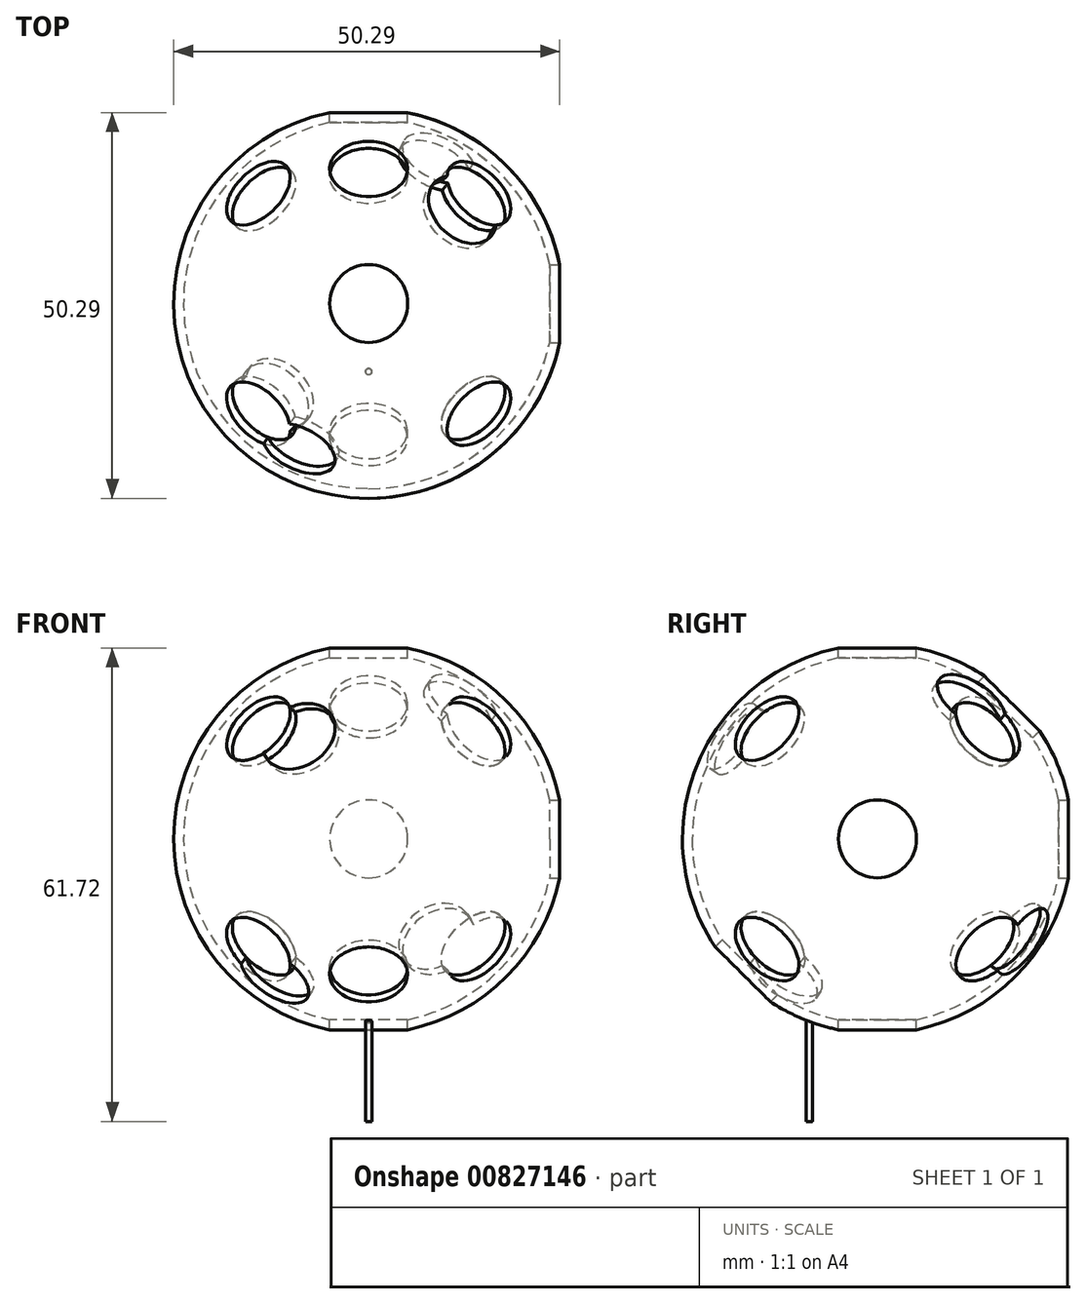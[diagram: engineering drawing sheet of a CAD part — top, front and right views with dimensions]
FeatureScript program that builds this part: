
annotation { "Feature Type Name" : "Feature", "Feature Type Description" : "" }
export const myFeature = defineFeature(function(context is Context, id is Id, definition is map)
    precondition{}
    {
        {
            assignVariable(context, id + "F0", {"name" : "SphereDiameter", "anyValue" : 2});
        }
        {
            var Q0;
            Q0=qCreatedBy(makeId("Top.planeOp"),FACE);
            var sketch = newSketch(context, id + "F1", { "sketchPlane" : qUnion([Q0])});
            skArc(sketch, "E0", {"start": v(0, 25.4) * mm, "mid": v(-25.4, 0) * mm, "end": v(0, -25.4) * mm});
            skLineSegment(sketch, "E1", {"start": v(0, 25.4) * mm, "end": v(0, -25.4) * mm});
            skSolve(sketch);
        }
        {
            var Q0;
            Q0=qSketchRegion(id+"F1",true);
            var Q1;
            Q1=sQuery(id+"F1.wireOp",EDGE,"E1");
            revolve(context, id + "F2", {"surfaceOperationType" : NewSurfaceOperationType.NEW, "entities" : qUnion([Q0]), "axis" : qUnion([Q1]), "revolveType" : RevolveType.FULL});
        }
        {
            var Q0;
            Q0=qCreatedBy(makeId("Top.planeOp"),FACE);
            var sketch = newSketch(context, id + "F3", { "sketchPlane" : qUnion([Q0])});
            skLineSegment(sketch, "E2", {"start": v(0, 0) * mm, "end": v(0, 25.4) * mm});
            skLineSegment(sketch, "E3", {"start": v(0, 0) * mm, "end": v(0, -25.4) * mm});
            skLineSegment(sketch, "E4", {"start": v(0, 0) * mm, "end": v(25.4, 0) * mm});
            skLineSegment(sketch, "E5", {"start": v(0, 0) * mm, "end": v(-25.4, 0) * mm});
            skSolve(sketch);
        }
        {
            var Q0;
            Q0=qCreatedBy(makeId("Front.planeOp"),FACE);
            var sketch = newSketch(context, id + "F4", { "sketchPlane" : qUnion([Q0])});
            skLineSegment(sketch, "E6", {"start": v(0, 0) * mm, "end": v(0, 25.4) * mm});
            skLineSegment(sketch, "E7", {"start": v(0, 0) * mm, "end": v(0, -25.4) * mm});
            skSolve(sketch);
        }
        {
            var Q0;
            Q0=sQuery(id+"F4.wireOp",VERTEX,"E6.end");
            var Q1;
            Q1=sQuery(id+"F3.wireOp",VERTEX,"E3.end");
            var Q2;
            Q2=sQuery(id+"F3.wireOp",VERTEX,"E4.end");
            cPlane(context, id + "F5", {"entities" : qUnion([Q0, Q1, Q2]), "cplaneType" : CPlaneType.THREE_POINT, "offset" : 25.4 * mm, "width" : 152.4 * mm, "height" : 152.4 * mm});
        }
        {
            var Q0;
            Q0=qCreatedBy(id+"F5.planeOp",FACE);
            var sketch = newSketch(context, id + "F6", { "sketchPlane" : qUnion([Q0])});
            skLineSegment(sketch, "E8", {"start": v(-20.74, 0) * mm, "end": v(10.37, -17.96) * mm});
            skLineSegment(sketch, "E9", {"start": v(10.37, -17.96) * mm, "end": v(10.37, 17.96) * mm});
            skLineSegment(sketch, "E10", {"start": v(10.37, 17.96) * mm, "end": v(-20.74, 0) * mm});
            skLineSegment(sketch, "E11", {"start": v(10.37, 17.96) * mm, "end": v(0, 0) * mm});
            skSolve(sketch);
        }
        {
            var Q0;
            Q0=sQuery(id+"F4.wireOp",VERTEX,"E6.end");
            var Q1;
            Q1=sQuery(id+"F6.wireOp",VERTEX,"E11.end");
            var Q2;
            Q2=sQuery(id+"F3.wireOp",VERTEX,"E3.start");
            cPlane(context, id + "F7", {"entities" : qUnion([Q0, Q1, Q2]), "cplaneType" : CPlaneType.THREE_POINT, "offset" : 25.4 * mm, "width" : 152.4 * mm, "height" : 152.4 * mm});
        }
        {
            var Q0;
            Q0=qCreatedBy(id+"F7.planeOp",FACE);
            var sketch = newSketch(context, id + "F8", { "sketchPlane" : qUnion([Q0])});
            skLineSegment(sketch, "E12", {"start": v(0, 0) * mm, "end": v(11.97, 8.47) * mm});
            skLineSegment(sketch, "E13", {"start": v(10.37, 7.33) * mm, "end": v(11.97, 8.47) * mm});
            skLineSegment(sketch, "E14", {"start": v(0, 0) * mm, "end": v(-10.37, -7.33) * mm});
            skSolve(sketch);
        }
        {
            var Q0;
            Q0=sQuery(id+"F3.wireOp",VERTEX,"E2.end");
            var Q1;
            Q1=sQuery(id+"F4.wireOp",VERTEX,"E6.end");
            var Q2;
            Q2=sQuery(id+"F3.wireOp",VERTEX,"E5.end");
            cPlane(context, id + "F9", {"entities" : qUnion([Q0, Q1, Q2]), "cplaneType" : CPlaneType.THREE_POINT, "offset" : 25.4 * mm, "width" : 152.4 * mm, "height" : 152.4 * mm});
        }
        {
            var Q0;
            Q0=qCreatedBy(id+"F9.planeOp",FACE);
            var sketch = newSketch(context, id + "F10", { "sketchPlane" : qUnion([Q0])});
            skLineSegment(sketch, "E15", {"start": v(20.74, 0) * mm, "end": v(-10.37, 17.96) * mm});
            skLineSegment(sketch, "E16", {"start": v(-10.37, 17.96) * mm, "end": v(-10.37, -17.96) * mm});
            skLineSegment(sketch, "E17", {"start": v(-10.37, -17.96) * mm, "end": v(20.74, 0) * mm});
            skLineSegment(sketch, "E18", {"start": v(-10.37, 17.96) * mm, "end": v(0, 0) * mm});
            skSolve(sketch);
        }
        {
            var Q0;
            Q0=sQuery(id+"F4.wireOp",VERTEX,"E6.end");
            var Q1;
            Q1=qCreatedBy(makeId("Origin.pointOp"),VERTEX);
            var Q2;
            Q2=sQuery(id+"F10.wireOp",VERTEX,"E18.end");
            cPlane(context, id + "F11", {"entities" : qUnion([Q0, Q1, Q2]), "cplaneType" : CPlaneType.THREE_POINT, "offset" : 25.4 * mm, "width" : 152.4 * mm, "height" : 152.4 * mm});
        }
        {
            var Q0;
            Q0=qCreatedBy(id+"F11.planeOp",FACE);
            var sketch = newSketch(context, id + "F12", { "sketchPlane" : qUnion([Q0])});
            skLineSegment(sketch, "E19", {"start": v(0, 0) * mm, "end": v(-11.97, 8.47) * mm});
            skLineSegment(sketch, "E20", {"start": v(-11.97, 8.47) * mm, "end": v(-10.37, 7.33) * mm});
            skLineSegment(sketch, "E21", {"start": v(10.37, -7.33) * mm, "end": v(0, 0) * mm});
            skSolve(sketch);
        }
        {
            var Q0;
            Q0=sQuery(id+"F3.wireOp",VERTEX,"E2.end");
            var Q1;
            Q1=sQuery(id+"F4.wireOp",VERTEX,"E7.end");
            var Q2;
            Q2=sQuery(id+"F3.wireOp",VERTEX,"E4.end");
            cPlane(context, id + "F13", {"entities" : qUnion([Q0, Q1, Q2]), "cplaneType" : CPlaneType.THREE_POINT, "offset" : 25.4 * mm, "width" : 152.4 * mm, "height" : 152.4 * mm});
        }
        {
            var Q0;
            Q0=qCreatedBy(id+"F13.planeOp",FACE);
            var sketch = newSketch(context, id + "F14", { "sketchPlane" : qUnion([Q0])});
            skLineSegment(sketch, "E22", {"start": v(10.37, -17.96) * mm, "end": v(10.37, 17.96) * mm});
            skLineSegment(sketch, "E23", {"start": v(10.37, 17.96) * mm, "end": v(-20.74, 0) * mm});
            skLineSegment(sketch, "E24", {"start": v(-20.74, 0) * mm, "end": v(10.37, -17.96) * mm});
            skLineSegment(sketch, "E25", {"start": v(10.37, 17.96) * mm, "end": v(0, 0) * mm});
            skSolve(sketch);
        }
        {
            var Q0;
            Q0=sQuery(id+"F3.wireOp",VERTEX,"E3.start");
            var Q1;
            Q1=sQuery(id+"F3.wireOp",VERTEX,"E2.end");
            var Q2;
            Q2=sQuery(id+"F14.wireOp",VERTEX,"E25.end");
            cPlane(context, id + "F15", {"entities" : qUnion([Q0, Q1, Q2]), "cplaneType" : CPlaneType.THREE_POINT, "offset" : 25.4 * mm, "width" : 152.4 * mm, "height" : 152.4 * mm});
        }
        {
            var Q0;
            Q0=qCreatedBy(id+"F15.planeOp",FACE);
            var sketch = newSketch(context, id + "F16", { "sketchPlane" : qUnion([Q0])});
            skLineSegment(sketch, "E26", {"start": v(0, 0) * mm, "end": v(8.47, -11.97) * mm});
            skLineSegment(sketch, "E27", {"start": v(7.33, -10.37) * mm, "end": v(8.47, -11.97) * mm});
            skLineSegment(sketch, "E28", {"start": v(0, 0) * mm, "end": v(-7.33, 10.37) * mm});
            skSolve(sketch);
        }
        {
            var Q0;
            Q0=sQuery(id+"F4.wireOp",VERTEX,"E6.end");
            var Q1;
            Q1=sQuery(id+"F3.wireOp",VERTEX,"E4.end");
            var Q2;
            Q2=sQuery(id+"F3.wireOp",VERTEX,"E2.end");
            cPlane(context, id + "F17", {"entities" : qUnion([Q0, Q1, Q2]), "cplaneType" : CPlaneType.THREE_POINT, "offset" : 25.4 * mm, "width" : 152.4 * mm, "height" : 152.4 * mm});
        }
        {
            var Q0;
            Q0=qCreatedBy(id+"F17.planeOp",FACE);
            var sketch = newSketch(context, id + "F18", { "sketchPlane" : qUnion([Q0])});
            skLineSegment(sketch, "E29", {"start": v(-10.37, 17.96) * mm, "end": v(20.74, 0) * mm});
            skLineSegment(sketch, "E30", {"start": v(20.74, 0) * mm, "end": v(-10.37, -17.96) * mm});
            skLineSegment(sketch, "E31", {"start": v(-10.37, -17.96) * mm, "end": v(-10.37, 17.96) * mm});
            skLineSegment(sketch, "E32", {"start": v(-10.37, 17.96) * mm, "end": v(0, 0) * mm});
            skSolve(sketch);
        }
        {
            var Q0;
            Q0=sQuery(id+"F4.wireOp",VERTEX,"E6.end");
            var Q1;
            Q1=sQuery(id+"F18.wireOp",VERTEX,"E32.end");
            var Q2;
            Q2=sQuery(id+"F3.wireOp",VERTEX,"E3.start");
            cPlane(context, id + "F19", {"entities" : qUnion([Q0, Q1, Q2]), "cplaneType" : CPlaneType.THREE_POINT, "offset" : 25.4 * mm, "width" : 152.4 * mm, "height" : 152.4 * mm});
        }
        {
            var Q0;
            Q0=qCreatedBy(id+"F19.planeOp",FACE);
            var sketch = newSketch(context, id + "F20", { "sketchPlane" : qUnion([Q0])});
            skLineSegment(sketch, "E33", {"start": v(0, 0) * mm, "end": v(11.97, 8.47) * mm});
            skLineSegment(sketch, "E34", {"start": v(10.37, 7.33) * mm, "end": v(11.97, 8.47) * mm});
            skLineSegment(sketch, "E35", {"start": v(0, 0) * mm, "end": v(-10.37, -7.33) * mm});
            skSolve(sketch);
        }
        {
            var Q0;
            Q0=qCreatedBy(makeId("Top.planeOp"),FACE);
            var Q1;
            Q1=sQuery(id+"F4.wireOp",VERTEX,"E6.end");
            cPlane(context, id + "F21", {"entities" : qUnion([Q0, Q1]), "cplaneType" : CPlaneType.PLANE_POINT, "offset" : 25.4 * mm, "width" : 152.4 * mm, "height" : 152.4 * mm});
        }
        {
            var Q0;
            Q0=qCreatedBy(id+"F21.planeOp",FACE);
            var sketch = newSketch(context, id + "F22", { "sketchPlane" : qUnion([Q0])});
            skCircle(sketch, "E36", {"center": v(0, 0) * mm, "radius": 5.08 * mm});
            skSolve(sketch);
        }
        {
            var Q0;
            Q0=qSketchRegion(id+"F22",true);
            extrude(context, id + "F23", {"entities" : qUnion([Q0]), "operationType" : NewBodyOperationType.REMOVE, "endBound" : BoundingType.SYMMETRIC, "oppositeDirection" : true, "depth" : 76.2 * mm, "offsetDistance" : 25.4 * mm});
        }
        {
            var Q0;
            Q0=qCreatedBy(makeId("Right.planeOp"),FACE);
            var Q1;
            Q1=sQuery(id+"F3.wireOp",VERTEX,"E4.end");
            cPlane(context, id + "F24", {"entities" : qUnion([Q0, Q1]), "cplaneType" : CPlaneType.PLANE_POINT, "offset" : 25.4 * mm, "width" : 152.4 * mm, "height" : 152.4 * mm});
        }
        {
            var Q0;
            Q0=qCreatedBy(id+"F24.planeOp",FACE);
            var sketch = newSketch(context, id + "F25", { "sketchPlane" : qUnion([Q0])});
            skCircle(sketch, "E37", {"center": v(0, 0) * mm, "radius": 5.08 * mm});
            skSolve(sketch);
        }
        {
            var Q0;
            Q0=qSketchRegion(id+"F25",true);
            extrude(context, id + "F26", {"entities" : qUnion([Q0]), "operationType" : NewBodyOperationType.REMOVE, "endBound" : BoundingType.SYMMETRIC, "oppositeDirection" : true, "depth" : 76.2 * mm, "offsetDistance" : 25.4 * mm});
        }
        {
            var Q0;
            Q0=qCreatedBy(makeId("Front.planeOp"),FACE);
            var Q1;
            Q1=sQuery(id+"F3.wireOp",VERTEX,"E2.end");
            cPlane(context, id + "F27", {"entities" : qUnion([Q0, Q1]), "cplaneType" : CPlaneType.PLANE_POINT, "offset" : 25.4 * mm, "width" : 152.4 * mm, "height" : 152.4 * mm});
        }
        {
            var Q0;
            Q0=qCreatedBy(id+"F27.planeOp",FACE);
            var sketch = newSketch(context, id + "F28", { "sketchPlane" : qUnion([Q0])});
            skCircle(sketch, "E38", {"center": v(0, 0) * mm, "radius": 5.08 * mm});
            skSolve(sketch);
        }
        {
            var Q0;
            Q0=qSketchRegion(id+"F28",true);
            extrude(context, id + "F29", {"entities" : qUnion([Q0]), "operationType" : NewBodyOperationType.REMOVE, "endBound" : BoundingType.SYMMETRIC, "depth" : 76.2 * mm, "offsetDistance" : 25.4 * mm});
        }
        {
            var Q0;
            Q0=qCreatedBy(id+"F5.planeOp",FACE);
            var Q1;
            Q1=sQuery(id+"F8.wireOp",VERTEX,"E13.end");
            cPlane(context, id + "F30", {"entities" : qUnion([Q0, Q1]), "cplaneType" : CPlaneType.PLANE_POINT, "offset" : 25.4 * mm, "width" : 152.4 * mm, "height" : 152.4 * mm});
        }
        {
            var Q0;
            Q0=qCreatedBy(id+"F30.planeOp",FACE);
            var sketch = newSketch(context, id + "F31", { "sketchPlane" : qUnion([Q0])});
            skCircle(sketch, "E39", {"center": v(0, 0) * mm, "radius": 5.08 * mm});
            skSolve(sketch);
        }
        {
            var Q0;
            Q0=qSketchRegion(id+"F31",true);
            extrude(context, id + "F32", {"entities" : qUnion([Q0]), "operationType" : NewBodyOperationType.REMOVE, "endBound" : BoundingType.SYMMETRIC, "depth" : 254 * mm, "offsetDistance" : 25.4 * mm});
        }
        {
            var Q0;
            Q0=qCreatedBy(id+"F9.planeOp",FACE);
            var Q1;
            Q1=sQuery(id+"F12.wireOp",VERTEX,"E20.start");
            cPlane(context, id + "F33", {"entities" : qUnion([Q0, Q1]), "cplaneType" : CPlaneType.PLANE_POINT, "offset" : 25.4 * mm, "width" : 152.4 * mm, "height" : 152.4 * mm});
        }
        {
            var Q0;
            Q0=qCreatedBy(id+"F33.planeOp",FACE);
            var sketch = newSketch(context, id + "F34", { "sketchPlane" : qUnion([Q0])});
            skCircle(sketch, "E40", {"center": v(0, 0) * mm, "radius": 5.08 * mm});
            skSolve(sketch);
        }
        {
            var Q0;
            Q0=qSketchRegion(id+"F34",true);
            extrude(context, id + "F35", {"entities" : qUnion([Q0]), "operationType" : NewBodyOperationType.REMOVE, "endBound" : BoundingType.SYMMETRIC, "depth" : 254 * mm, "offsetDistance" : 25.4 * mm});
        }
        {
            var Q0;
            Q0=qCreatedBy(id+"F17.planeOp",FACE);
            var Q1;
            Q1=sQuery(id+"F20.wireOp",VERTEX,"E34.end");
            cPlane(context, id + "F36", {"entities" : qUnion([Q0, Q1]), "cplaneType" : CPlaneType.PLANE_POINT, "offset" : 25.4 * mm, "width" : 152.4 * mm, "height" : 152.4 * mm});
        }
        {
            var Q0;
            Q0=qCreatedBy(id+"F36.planeOp",FACE);
            var sketch = newSketch(context, id + "F37", { "sketchPlane" : qUnion([Q0])});
            skCircle(sketch, "E41", {"center": v(0, 0) * mm, "radius": 5.08 * mm});
            skSolve(sketch);
        }
        {
            var Q0;
            Q0=qSketchRegion(id+"F37",true);
            extrude(context, id + "F38", {"entities" : qUnion([Q0]), "operationType" : NewBodyOperationType.REMOVE, "endBound" : BoundingType.SYMMETRIC, "depth" : 254 * mm, "offsetDistance" : 25.4 * mm});
        }
        {
            var Q0;
            Q0=qCreatedBy(id+"F13.planeOp",FACE);
            var Q1;
            Q1=sQuery(id+"F16.wireOp",VERTEX,"E27.end");
            cPlane(context, id + "F39", {"entities" : qUnion([Q0, Q1]), "cplaneType" : CPlaneType.PLANE_POINT, "offset" : 25.4 * mm, "width" : 152.4 * mm, "height" : 152.4 * mm});
        }
        {
            var Q0;
            Q0=qCreatedBy(id+"F39.planeOp",FACE);
            var sketch = newSketch(context, id + "F40", { "sketchPlane" : qUnion([Q0])});
            skCircle(sketch, "E42", {"center": v(0, 0) * mm, "radius": 5.08 * mm});
            skSolve(sketch);
        }
        {
            var Q0;
            Q0=qSketchRegion(id+"F40",true);
            extrude(context, id + "F41", {"entities" : qUnion([Q0]), "operationType" : NewBodyOperationType.REMOVE, "endBound" : BoundingType.SYMMETRIC, "depth" : 254 * mm, "offsetDistance" : 25.4 * mm});
        }
        {
            var Q0;
            Q0=qCreatedBy(makeId("Top.planeOp"),FACE);
            var sketch = newSketch(context, id + "F42", { "sketchPlane" : qUnion([Q0])});
            skArc(sketch, "E43", {"start": v(0, 24.13) * mm, "mid": v(-24.13, 0) * mm, "end": v(0, -24.13) * mm});
            skLineSegment(sketch, "E44", {"start": v(0, 24.13) * mm, "end": v(0, -24.13) * mm});
            skSolve(sketch);
        }
        {
            var Q0;
            Q0=qSketchRegion(id+"F42",true);
            var Q1;
            Q1=sQuery(id+"F3.wireOp",EDGE,"E2");
            revolve(context, id + "F43", {"operationType" : NewBodyOperationType.REMOVE, "surfaceOperationType" : NewSurfaceOperationType.NEW, "entities" : qUnion([Q0]), "axis" : qUnion([Q1]), "revolveType" : RevolveType.FULL, "oppositeDirection" : true});
        }
        {
            var Q0;
            Q0=sQuery(id+"F12.wireOp",VERTEX,"E20.start");
            var Q1;
            Q1=sQuery(id+"F28.wireOp",VERTEX,"E38.center");
            var Q2;
            Q2=sQuery(id+"F20.wireOp",VERTEX,"E34.end");
            cPlane(context, id + "F44", {"entities" : qUnion([Q0, Q1, Q2]), "cplaneType" : CPlaneType.THREE_POINT, "offset" : 25.4 * mm, "width" : 152.4 * mm, "height" : 152.4 * mm});
        }
        {
            var Q0;
            Q0=qCreatedBy(id+"F44.planeOp",FACE);
            var sketch = newSketch(context, id + "F45", { "sketchPlane" : qUnion([Q0])});
            skLineSegment(sketch, "E45", {"start": v(7.33, 4.04) * mm, "end": v(-7.33, 4.04) * mm});
            skLineSegment(sketch, "E46", {"start": v(0, 23.54) * mm, "end": v(0, 4.04) * mm});
            skSolve(sketch);
        }
        {
            var Q0;
            Q0=sQuery(id+"F4.wireOp",VERTEX,"E6.end");
            var Q1;
            Q1=sQuery(id+"F20.wireOp",VERTEX,"E34.end");
            var Q2;
            Q2=sQuery(id+"F12.wireOp",VERTEX,"E20.start");
            cPlane(context, id + "F46", {"entities" : qUnion([Q0, Q1, Q2]), "cplaneType" : CPlaneType.THREE_POINT, "offset" : 25.4 * mm, "width" : 152.4 * mm, "height" : 152.4 * mm});
        }
        {
            var Q0;
            Q0=qCreatedBy(id+"F46.planeOp",FACE);
            var sketch = newSketch(context, id + "F47", { "sketchPlane" : qUnion([Q0])});
            skLineSegment(sketch, "E47", {"start": v(0, 23.54) * mm, "end": v(0, 4.04) * mm});
            skSolve(sketch);
        }
        {
            var Q0;
            Q0=qCreatedBy(id+"F46.planeOp",FACE);
            var sketch = newSketch(context, id + "F48", { "sketchPlane" : qUnion([Q0])});
            skLineSegment(sketch, "E48", {"start": v(0, -3.88) * mm, "end": v(0, 4.04) * mm});
            skSolve(sketch);
        }
        {
            var Q0;
            Q0=qCreatedBy(id+"F44.planeOp",FACE);
            var sketch = newSketch(context, id + "F49", { "sketchPlane" : qUnion([Q0])});
            skLineSegment(sketch, "E49", {"start": v(0, 4.04) * mm, "end": v(0, -3.88) * mm});
            skSolve(sketch);
        }
        {
            var Q0;
            Q0=sQuery(id+"F12.wireOp",VERTEX,"E19.start");
            var Q1;
            Q1=sQuery(id+"F12.wireOp",VERTEX,"E20.start");
            var Q2;
            Q2=sQuery(id+"F20.wireOp",VERTEX,"E34.end");
            cPlane(context, id + "F50", {"entities" : qUnion([Q0, Q1, Q2]), "cplaneType" : CPlaneType.THREE_POINT, "offset" : 25.4 * mm, "width" : 152.4 * mm, "height" : 152.4 * mm});
        }
        {
            var Q0;
            Q0=sQuery(id+"F49.wireOp",VERTEX,"E49.start");
            var Q1;
            Q1=sQuery(id+"F48.wireOp",VERTEX,"E48.start");
            var Q2;
            Q2=sQuery(id+"F48.wireOp",VERTEX,"E48.end");
            cPlane(context, id + "F51", {"entities" : qUnion([Q0, Q1, Q2]), "cplaneType" : CPlaneType.THREE_POINT, "offset" : 25.4 * mm, "width" : 152.4 * mm, "height" : 152.4 * mm});
        }
        {
            var Q0;
            Q0=qCreatedBy(id+"F51.planeOp",FACE);
            var sketch = newSketch(context, id + "F52", { "sketchPlane" : qUnion([Q0])});
            skLineSegment(sketch, "E50", {"start": v(1.61, 15.15) * mm, "end": v(15.53, 1.33) * mm});
            skSolve(sketch);
        }
        {
            var Q0;
            Q0=sQuery(id+"F52.wireOp",EDGE,"E50");
            var Q1;
            Q1=qCreatedBy(id+"F44.planeOp",FACE);
            cPlane(context, id + "F53", {"entities" : qUnion([Q0, Q1]), "cplaneType" : CPlaneType.LINE_ANGLE, "offset" : 25.4 * mm, "angle" : 0 * degree, "width" : 152.4 * mm, "height" : 152.4 * mm});
        }
        {
            var Q0;
            Q0=qCreatedBy(id+"F53.planeOp",FACE);
            var sketch = newSketch(context, id + "F54", { "sketchPlane" : qUnion([Q0])});
            skCircle(sketch, "E51", {"center": v(0, 0) * mm, "radius": 5.08 * mm});
            skSolve(sketch);
        }
        {
            var Q0;
            Q0=qSketchRegion(id+"F54",true);
            extrude(context, id + "F55", {"entities" : qUnion([Q0]), "operationType" : NewBodyOperationType.REMOVE, "endBound" : BoundingType.SYMMETRIC, "depth" : 127 * mm, "offsetDistance" : 25.4 * mm});
        }
        {
            var Q0;
            Q0=sQuery(id+"F8.wireOp",VERTEX,"E13.end");
            var Q1;
            Q1=qCreatedBy(makeId("Origin.pointOp"),VERTEX);
            var Q2;
            Q2=sQuery(id+"F20.wireOp",VERTEX,"E34.end");
            cPlane(context, id + "F56", {"entities" : qUnion([Q0, Q1, Q2]), "cplaneType" : CPlaneType.THREE_POINT, "offset" : 25.4 * mm, "width" : 152.4 * mm, "height" : 152.4 * mm});
        }
        {
            var Q0;
            Q0=qCreatedBy(id+"F56.planeOp",FACE);
            var sketch = newSketch(context, id + "F57", { "sketchPlane" : qUnion([Q0])});
            skLineSegment(sketch, "E52", {"start": v(10.37, 7.33) * mm, "end": v(10.37, -7.33) * mm});
            skLineSegment(sketch, "E53", {"start": v(0, 0) * mm, "end": v(10.37, 0) * mm});
            skSolve(sketch);
        }
        {
            var Q0;
            Q0=sQuery(id+"F57.wireOp",VERTEX,"E53.end");
            var Q1;
            Q1=sQuery(id+"F4.wireOp",VERTEX,"E6.end");
            var Q2;
            Q2=sQuery(id+"F8.wireOp",VERTEX,"E12.start");
            cPlane(context, id + "F58", {"entities" : qUnion([Q0, Q1, Q2]), "cplaneType" : CPlaneType.THREE_POINT, "offset" : 25.4 * mm, "width" : 152.4 * mm, "height" : 152.4 * mm});
        }
        {
            var Q0;
            Q0=qCreatedBy(id+"F58.planeOp",FACE);
            var sketch = newSketch(context, id + "F59", { "sketchPlane" : qUnion([Q0])});
            skLineSegment(sketch, "E54", {"start": v(-7.33, 7.33) * mm, "end": v(0, 25.4) * mm});
            skLineSegment(sketch, "E55", {"start": v(-7.33, 7.33) * mm, "end": v(-25.4, 0) * mm});
            skLineSegment(sketch, "E56", {"start": v(0, 14.66) * mm, "end": v(-14.66, 0) * mm});
            skSolve(sketch);
        }
        {
            var Q0;
            Q0=sQuery(id+"F57.wireOp",VERTEX,"E53.end");
            var Q1;
            Q1=sQuery(id+"F59.wireOp",VERTEX,"E56.start");
            var Q2;
            Q2=sQuery(id+"F8.wireOp",VERTEX,"E13.end");
            cPlane(context, id + "F60", {"entities" : qUnion([Q0, Q1, Q2]), "cplaneType" : CPlaneType.THREE_POINT, "offset" : 25.4 * mm, "width" : 152.4 * mm, "height" : 152.4 * mm});
        }
        {
            var Q0;
            Q0=qCreatedBy(id+"F60.planeOp",FACE);
            var sketch = newSketch(context, id + "F61", { "sketchPlane" : qUnion([Q0])});
            skCircle(sketch, "E57", {"center": v(0, 0) * mm, "radius": 5.08 * mm});
            skSolve(sketch);
        }
        {
            var Q0;
            Q0=qSketchRegion(id+"F61",true);
            extrude(context, id + "F62", {"entities" : qUnion([Q0]), "operationType" : NewBodyOperationType.REMOVE, "endBound" : BoundingType.SYMMETRIC, "depth" : 127 * mm, "offsetDistance" : 25.4 * mm});
        }
        {
            var Q0;
            Q0=sQuery(id+"F3.wireOp",VERTEX,"E5.end");
            var Q1;
            Q1=qCreatedBy(makeId("Origin.pointOp"),VERTEX);
            var Q2;
            Q2=sQuery(id+"F3.wireOp",VERTEX,"E3.end");
            cPlane(context, id + "F63", {"entities" : qUnion([Q0, Q1, Q2]), "cplaneType" : CPlaneType.THREE_POINT, "offset" : 25.4 * mm, "width" : 152.4 * mm, "height" : 152.4 * mm});
        }
        {
            var Q0;
            Q0=qCreatedBy(id+"F63.planeOp",FACE);
            var sketch = newSketch(context, id + "F64", { "sketchPlane" : qUnion([Q0])});
            skLineSegment(sketch, "E58", {"start": v(0, -25.4) * mm, "end": v(-25.4, 0) * mm});
            skLineSegment(sketch, "E59", {"start": v(0, 0) * mm, "end": v(-12.7, -12.7) * mm});
            skSolve(sketch);
        }
        {
            var Q0;
            Q0=sQuery(id+"F16.wireOp",VERTEX,"E28.end");
            var Q1;
            Q1=sQuery(id+"F20.wireOp",VERTEX,"E35.end");
            var Q2;
            Q2=sQuery(id+"F57.wireOp",VERTEX,"E53.start");
            cPlane(context, id + "F65", {"entities" : qUnion([Q0, Q1, Q2]), "cplaneType" : CPlaneType.THREE_POINT, "offset" : 25.4 * mm, "width" : 152.4 * mm, "height" : 152.4 * mm});
        }
        {
            var Q0;
            Q0=qCreatedBy(id+"F65.planeOp",FACE);
            var sketch = newSketch(context, id + "F66", { "sketchPlane" : qUnion([Q0])});
            skLineSegment(sketch, "E60", {"start": v(10.37, -7.33) * mm, "end": v(10.37, 7.33) * mm});
            skLineSegment(sketch, "E61", {"start": v(10.37, 0) * mm, "end": v(17.96, 0) * mm});
            skPoint(sketch, "E61.endSnap0", {"position": v(10.37, 0) * mm});
            skSolve(sketch);
        }
        {
            var Q0;
            Q0=qCreatedBy(id+"F63.planeOp",FACE);
            var sketch = newSketch(context, id + "F67", { "sketchPlane" : qUnion([Q0])});
            skLineSegment(sketch, "E62", {"start": v(-14.66, 0) * mm, "end": v(0, -14.66) * mm});
            skLineSegment(sketch, "E63", {"start": v(-14.66, 0) * mm, "end": v(-25.4, 0) * mm});
            skLineSegment(sketch, "E64", {"start": v(-14.66, 0) * mm, "end": v(-14.66, 0) * mm});
            skLineSegment(sketch, "E65", {"start": v(0, -14.66) * mm, "end": v(0, -25.4) * mm});
            skSolve(sketch);
        }
        {
            var Q0;
            Q0=sQuery(id+"F67.wireOp",VERTEX,"E63.end");
            var Q1;
            Q1=sQuery(id+"F67.wireOp",VERTEX,"E65.end");
            var Q2;
            Q2=sQuery(id+"F20.wireOp",VERTEX,"E35.end");
            cPlane(context, id + "F68", {"entities" : qUnion([Q0, Q1, Q2]), "cplaneType" : CPlaneType.THREE_POINT, "offset" : 25.4 * mm, "width" : 152.4 * mm, "height" : 152.4 * mm});
        }
        {
            var Q0;
            Q0=qCreatedBy(id+"F68.planeOp",FACE);
            var sketch = newSketch(context, id + "F69", { "sketchPlane" : qUnion([Q0])});
            skCircle(sketch, "E66", {"center": v(0, 0) * mm, "radius": 5.08 * mm});
            skSolve(sketch);
        }
        {
            var Q0;
            Q0=qSketchRegion(id+"F69",true);
            extrude(context, id + "F70", {"entities" : qUnion([Q0]), "operationType" : NewBodyOperationType.REMOVE, "endBound" : BoundingType.SYMMETRIC, "oppositeDirection" : true, "depth" : 101.6 * mm, "offsetDistance" : 25.4 * mm});
        }
        {
            var Q0;
            Q0=qCreatedBy(makeId("Top.planeOp"),FACE);
            cPlane(context, id + "F71", {"entities" : qUnion([Q0]), "cplaneType" : CPlaneType.OFFSET, "offset" : ((getVariable(context, 'SphereDiameter') / 2) - (getVariable(context, 'SphereDiameter') / 90)) * mm, "oppositeDirection" : true, "width" : 152.4 * mm, "height" : 152.4 * mm});
        }
        {
            var Q0;
            Q0=qCreatedBy(id+"F71.planeOp",FACE);
            var sketch = newSketch(context, id + "F72", { "sketchPlane" : qUnion([Q0])});
            skCircle(sketch, "E67", {"center": v(0, 0) * mm, "radius": 5.08 * mm});
            skCircle(sketch, "E68", {"center": v(0, 0) * mm, "radius": 2.86 * mm});
            skSolve(sketch);
        }
        {
            var Q0;
            Q0=qCreatedBy(makeId("Top.planeOp"),FACE);
            var sketch = newSketch(context, id + "F73", { "sketchPlane" : qUnion([Q0])});
            skCircle(sketch, "E69", {"center": v(0, 0) * mm, "radius": 5.08 * mm});
            skSolve(sketch);
        }
        {
            var Q0;
            Q0=qSketchRegion(id+"F73",true);
            extrude(context, id + "F74", {"entities" : qUnion([Q0]), "operationType" : NewBodyOperationType.REMOVE, "endBound" : BoundingType.THROUGH_ALL, "oppositeDirection" : true, "depth" : (getVariable(context, 'SphereDiameter') * 3) * mm, "offsetDistance" : 25.4 * mm});
        }
        {
            var Q0;
            Q0=qCreatedBy(makeId("Top.planeOp"),FACE);
            cPlane(context, id + "F75", {"entities" : qUnion([Q0]), "cplaneType" : CPlaneType.OFFSET, "offset" : 22.86 * mm, "oppositeDirection" : true, "width" : 152.4 * mm, "height" : 152.4 * mm});
        }
        {
            var Q0;
            Q0=qCreatedBy(id+"F75.planeOp",FACE);
            var sketch = newSketch(context, id + "F76", { "sketchPlane" : qUnion([Q0])});
            skCircle(sketch, "E70", {"center": v(0, -8.9) * mm, "radius": 0.4 * mm});
            skSolve(sketch);
        }
        {
            var Q0;
            Q0=qSketchRegion(id+"F76",true);
            extrude(context, id + "F77", {"entities" : qUnion([Q0]), "operationType" : NewBodyOperationType.ADD, "oppositeDirection" : true, "depth" : 13.97 * mm, "offsetDistance" : 25.4 * mm});
        }
        {
            var Q0;
            Q0=qCreatedBy(makeId("Front.planeOp"),FACE);
            var sketch = newSketch(context, id + "F78", { "sketchPlane" : qUnion([Q0])});
            skLineSegment(sketch, "E71", {"start": v(0, -37.84) * mm, "end": v(0, 0) * mm});
            skSolve(sketch);
        }
    });
